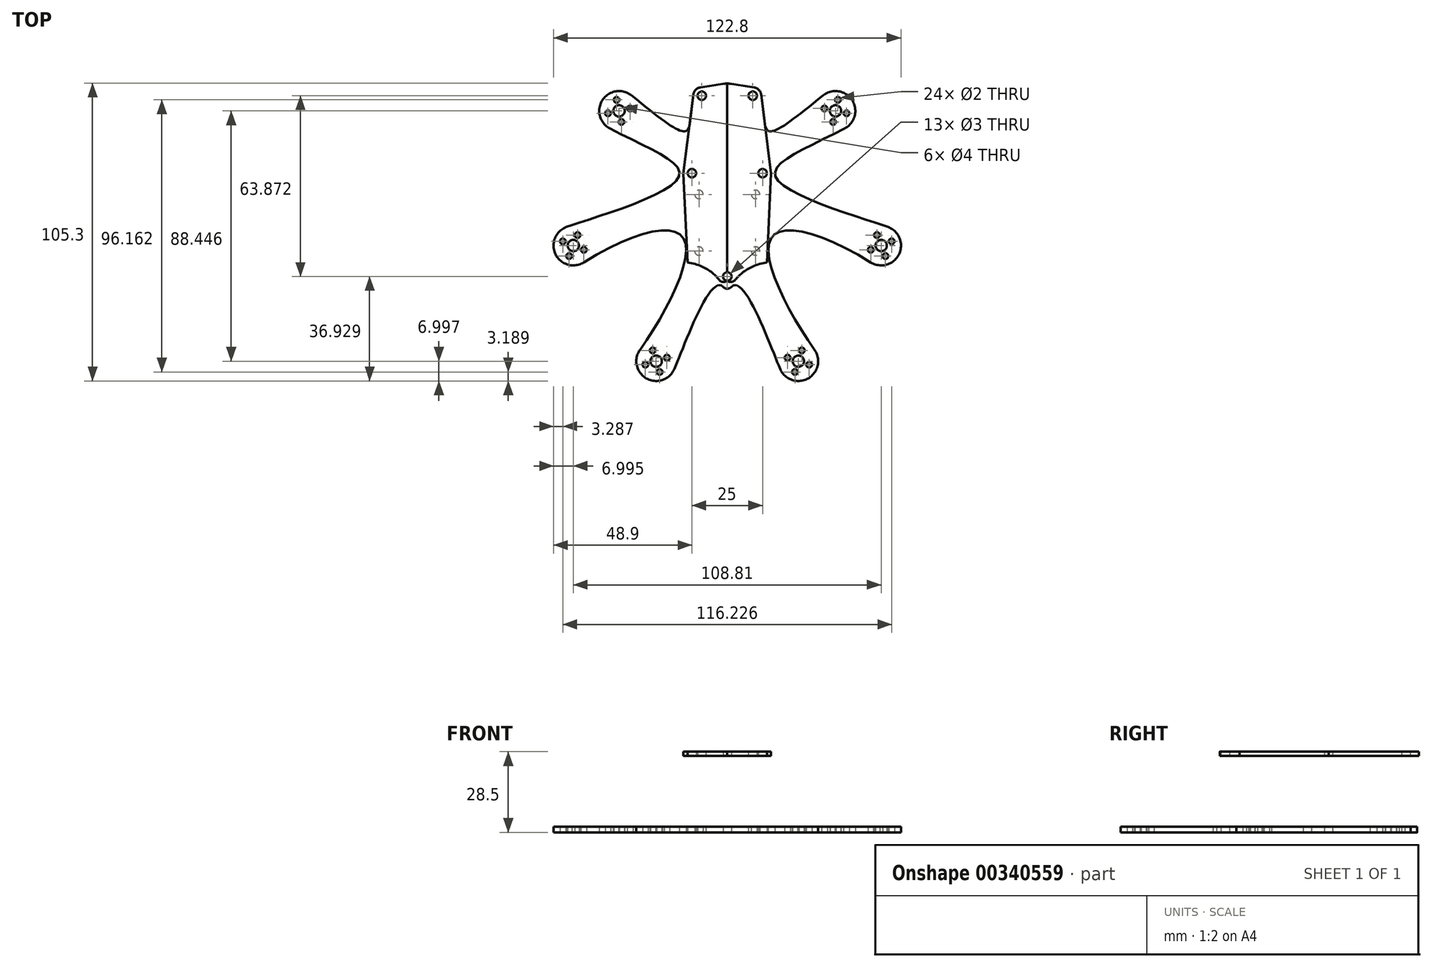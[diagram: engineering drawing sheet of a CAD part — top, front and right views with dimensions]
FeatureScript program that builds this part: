
annotation { "Feature Type Name" : "Feature", "Feature Type Description" : "" }
export const myFeature = defineFeature(function(context is Context, id is Id, definition is map)
    precondition{}
    {
        {
            var Q0;
            Q0=qCreatedBy(makeId("Top.planeOp"),FACE);
            var sketch = newSketch(context, id + "F0", { "sketchPlane" : qUnion([Q0])});
            skCircle(sketch, "E0", {"center": v(0, 0) * mm, "radius": 55 * mm, "construction": true});
            skCircle(sketch, "E1", {"center": v(-38.25, 39.52) * mm, "radius": 24.13 * mm, "construction": true});
            skCircle(sketch, "E2", {"center": v(-54.4, -8.07) * mm, "radius": 24.13 * mm, "construction": true});
            skCircle(sketch, "E3", {"center": v(-25.13, -48.92) * mm, "radius": 24.13 * mm, "construction": true});
            skLineSegment(sketch, "E4.bottom", {"start": v(13.5, -13.5) * mm, "end": v(-13.5, -13.5) * mm, "construction": true});
            skLineSegment(sketch, "E4.top", {"start": v(13.5, 13.5) * mm, "end": v(-13.5, 13.5) * mm, "construction": true});
            skLineSegment(sketch, "E4.left", {"start": v(13.5, -13.5) * mm, "end": v(13.5, 13.5) * mm, "construction": true});
            skLineSegment(sketch, "E4.right", {"start": v(-13.5, -13.5) * mm, "end": v(-13.5, 13.5) * mm, "construction": true});
            skLineSegment(sketch, "E5", {"start": v(-38.25, 39.52) * mm, "end": v(0, 15) * mm, "construction": true});
            skCircle(sketch, "E6", {"center": v(-38.25, 39.52) * mm, "radius": 7 * mm});
            skCircle(sketch, "E7", {"center": v(-54.4, -8.07) * mm, "radius": 7 * mm});
            skCircle(sketch, "E8", {"center": v(-25.13, -48.92) * mm, "radius": 7 * mm});
            skLineSegment(sketch, "E9", {"start": v(-26.46, 31.97) * mm, "end": v(-23.5, 36.6) * mm, "construction": true});
            skLineSegment(sketch, "E10", {"start": v(-23.5, 36.6) * mm, "end": v(-8.34, 26.88) * mm, "construction": true});
            skLineSegment(sketch, "E11", {"start": v(-8.34, 26.88) * mm, "end": v(-14.28, 17.62) * mm, "construction": true});
            skLineSegment(sketch, "E12", {"start": v(-14.28, 17.62) * mm, "end": v(-29.43, 27.34) * mm, "construction": true});
            skLineSegment(sketch, "E13", {"start": v(-29.43, 27.34) * mm, "end": v(-26.46, 31.97) * mm, "construction": true});
            skLineSegment(sketch, "E14", {"start": v(-54.4, -8.07) * mm, "end": v(0, 15) * mm, "construction": true});
            skLineSegment(sketch, "E15", {"start": v(-41.52, -2.6) * mm, "end": v(-43.66, 2.46) * mm, "construction": true});
            skLineSegment(sketch, "E16", {"start": v(-43.66, 2.46) * mm, "end": v(-27.1, 9.49) * mm, "construction": true});
            skLineSegment(sketch, "E17", {"start": v(-27.1, 9.49) * mm, "end": v(-22.8, -0.64) * mm, "construction": true});
            skLineSegment(sketch, "E18", {"start": v(-22.8, -0.64) * mm, "end": v(-39.37, -7.67) * mm, "construction": true});
            skLineSegment(sketch, "E19", {"start": v(-39.37, -7.67) * mm, "end": v(-41.52, -2.6) * mm, "construction": true});
            skLineSegment(sketch, "E20", {"start": v(-25.13, -48.92) * mm, "end": v(0, 0) * mm, "construction": true});
            skLineSegment(sketch, "E21", {"start": v(-18.73, -36.47) * mm, "end": v(-23.63, -33.96) * mm, "construction": true});
            skLineSegment(sketch, "E22", {"start": v(-23.63, -33.96) * mm, "end": v(-15.4, -17.95) * mm, "construction": true});
            skLineSegment(sketch, "E23", {"start": v(-15.4, -17.95) * mm, "end": v(-5.62, -22.97) * mm, "construction": true});
            skLineSegment(sketch, "E24", {"start": v(-5.62, -22.97) * mm, "end": v(-13.84, -38.98) * mm, "construction": true});
            skLineSegment(sketch, "E25", {"start": v(-13.84, -38.98) * mm, "end": v(-18.73, -36.47) * mm, "construction": true});
            skPoint(sketch, "E26", {"position": v(0, 13.5) * mm});
            skLineSegment(sketch, "E27", {"start": v(-14.28, 17.62) * mm, "end": v(-27.1, 9.49) * mm, "construction": true});
            skLineSegment(sketch, "E28", {"start": v(-22.8, -0.64) * mm, "end": v(-15.4, -17.95) * mm, "construction": true});
            skFitSpline(sketch, "E29", {"points": [v(-56.9, -1.53) * mm, v(-17.37, 15.66) * mm, v(-41.5, 33.32) * mm], "startDerivative": vector(36.2, 13.81) * mm, "endDerivative": vector(-89.8, 47.04) * mm});
            skFitSpline(sketch, "E30", {"points": [v(-50.68, -14) * mm, v(-15.32, -5.8) * mm, v(-30.82, -44.85) * mm], "startDerivative": vector(104.9, 65.91) * mm, "endDerivative": vector(-53.34, -74.52) * mm});
            skFitSpline(sketch, "E31", {"points": [v(-18.7, -51.71) * mm, v(0, -25.5) * mm], "startDerivative": vector(11.94, 27.48) * mm, "endDerivative": vector(12.67, -40.7) * mm});
            skLineSegment(sketch, "E32.bottom", {"start": v(10, 39.13) * mm, "end": v(-10, 39.13) * mm, "construction": true});
            skLineSegment(sketch, "E32.top", {"start": v(10, 29.13) * mm, "end": v(-10, 29.13) * mm, "construction": true});
            skLineSegment(sketch, "E32.left", {"start": v(10, 39.13) * mm, "end": v(10, 29.13) * mm, "construction": true});
            skLineSegment(sketch, "E32.right", {"start": v(-10, 39.13) * mm, "end": v(-10, 29.13) * mm, "construction": true});
            skPoint(sketch, "E32.middle", {"position": v(0, 34.13) * mm});
            skCircle(sketch, "E33", {"center": v(-9, 44.88) * mm, "radius": 2.5 * mm, "construction": true});
            skCircle(sketch, "E34", {"center": v(0, -19) * mm, "radius": 2.5 * mm, "construction": true});
            skCircle(sketch, "E35", {"center": v(-12.5, 17.5) * mm, "radius": 2.5 * mm, "construction": true});
            skLineSegment(sketch, "E36", {"start": v(-11.98, 45.26) * mm, "end": v(-15.5, 17.5) * mm});
            skLineSegment(sketch, "E37", {"start": v(-9.48, 47.84) * mm, "end": v(0, 49.38) * mm});
            skArc(sketch, "E38", {"start": v(-9, 41.88) * mm, "mid": v(-11.12, 47) * mm, "end": v(-6, 44.88) * mm});
            skFitSpline(sketch, "E39", {"points": [v(-33.86, 44.98) * mm, v(-13.3, 34.86) * mm], "startDerivative": vector(41.25, -33.22) * mm, "endDerivative": vector(2.26, 17.82) * mm});
            skCircle(sketch, "E40", {"center": v(0, -19) * mm, "radius": 1.5 * mm});
            skCircle(sketch, "E41", {"center": v(-12.5, 17.5) * mm, "radius": 1.5 * mm});
            skCircle(sketch, "E42", {"center": v(-9, 44.88) * mm, "radius": 1.5 * mm});
            skLineSegment(sketch, "E43", {"start": v(-15.5, 17.5) * mm, "end": v(-14.02, -14) * mm});
            skFitSpline(sketch, "E44", {"points": [v(-14.02, -14) * mm, v(0, -25.5) * mm], "startDerivative": vector(26.66, -3.76) * mm, "endDerivative": vector(2.8, -10.93) * mm});
            skLineSegment(sketch, "E45", {"start": v(0, 49.38) * mm, "end": v(0, -25.5) * mm});
            skCircle(sketch, "E46", {"center": v(-38.25, 39.52) * mm, "radius": 2 * mm});
            skCircle(sketch, "E47", {"center": v(-54.4, -8.07) * mm, "radius": 2 * mm});
            skCircle(sketch, "E48", {"center": v(-25.13, -48.92) * mm, "radius": 2 * mm});
            skLineSegment(sketch, "E49", {"start": v(-38.25, 39.52) * mm, "end": v(-34.34, 40.38) * mm, "construction": true});
            skCircle(sketch, "E50", {"center": v(-34.34, 40.38) * mm, "radius": 1 * mm});
            skCircle(sketch, "E51.1.0", {"center": v(-39.1, 43.43) * mm, "radius": 1 * mm});
            skCircle(sketch, "E51.2.0", {"center": v(-42.16, 38.67) * mm, "radius": 1 * mm});
            skCircle(sketch, "E51.3.0", {"center": v(-37.4, 35.62) * mm, "radius": 1 * mm});
            skLineSegment(sketch, "E52", {"start": v(-54.4, -8.07) * mm, "end": v(-52.9, -4.36) * mm, "construction": true});
            skCircle(sketch, "E53", {"center": v(-52.9, -4.36) * mm, "radius": 1 * mm});
            skCircle(sketch, "E54.1.0", {"center": v(-58.11, -6.57) * mm, "radius": 1 * mm});
            skCircle(sketch, "E54.2.0", {"center": v(-55.9, -11.78) * mm, "radius": 1 * mm});
            skCircle(sketch, "E54.3.0", {"center": v(-50.7, -9.57) * mm, "radius": 1 * mm});
            skLineSegment(sketch, "E55", {"start": v(-25.13, -48.92) * mm, "end": v(-26.35, -45.11) * mm, "construction": true});
            skCircle(sketch, "E56", {"center": v(-26.35, -45.11) * mm, "radius": 1 * mm});
            skCircle(sketch, "E57.1.0", {"center": v(-28.94, -50.15) * mm, "radius": 1 * mm});
            skCircle(sketch, "E57.2.0", {"center": v(-23.9, -52.73) * mm, "radius": 1 * mm});
            skCircle(sketch, "E57.3.0", {"center": v(-21.32, -47.7) * mm, "radius": 1 * mm});
            skCircle(sketch, "E58", {"center": v(-10, 10) * mm, "radius": 1.5 * mm});
            skCircle(sketch, "E59", {"center": v(-10, -10) * mm, "radius": 1.5 * mm});
            skSolve(sketch);
        }
        {
            var Q0;
            {var subQ0=sQuery(id+"F0.wireOp",EDGE,"E6");var subQ1=makeQuery(id+"F0.imprint","INTERSECT",VERTEX,{"derivedFrom":[subQ0,sQuery(id+"F0.wireOp",EDGE,"E29")]});Q0=makeQuery(id+"F0.imprint","IMPRINT",FACE,{"disambiguationData":[TD([[makeQuery(id+"F0.imprint","IMPRINT",EDGE,{"disambiguationData":[TD([[subQ1,1.0]])],"derivedFrom":subQ0}),1.0]])]});}
            var Q1;
            {var subQ0=sQuery(id+"F0.wireOp",EDGE,"E7");var subQ1=makeQuery(id+"F0.imprint","INTERSECT",VERTEX,{"derivedFrom":[subQ0,sQuery(id+"F0.wireOp",EDGE,"E29")]});Q1=makeQuery(id+"F0.imprint","IMPRINT",FACE,{"disambiguationData":[TD([[makeQuery(id+"F0.imprint","IMPRINT",EDGE,{"disambiguationData":[TD([[subQ1,-1.0]])],"derivedFrom":subQ0}),1.0]])]});}
            var Q2;
            {var subQ0=sQuery(id+"F0.wireOp",EDGE,"E8");var subQ1=makeQuery(id+"F0.imprint","INTERSECT",VERTEX,{"derivedFrom":[subQ0,sQuery(id+"F0.wireOp",EDGE,"E30")]});Q2=makeQuery(id+"F0.imprint","IMPRINT",FACE,{"disambiguationData":[TD([[makeQuery(id+"F0.imprint","IMPRINT",EDGE,{"disambiguationData":[TD([[subQ1,-1.0]])],"derivedFrom":subQ0}),1.0]])]});}
            var Q3;
            {var subQ3=sQuery(id+"F0.wireOp",EDGE,"E29");Q3=makeQuery(id+"F0.imprint","IMPRINT",FACE,{"disambiguationData":[TD([[makeQuery(id+"F0.imprint","IMPRINT",EDGE,{"derivedFrom":subQ3}),-1.0]])]});}
            var Q4;
            {var subQ6=sQuery(id+"F0.wireOp",EDGE,"E37");Q4=makeQuery(id+"F0.imprint","IMPRINT",FACE,{"disambiguationData":[TD([[makeQuery(id+"F0.imprint","IMPRINT",EDGE,{"derivedFrom":subQ6}),-1.0]])]});}
            extrude(context, id + "F1", {"entities" : qUnion([Q0, Q1, Q2, Q3, Q4]), "depth" : 2 * mm});
        }
        {
            var Q0;
            Q0=makeQuery(id+"F1.opExtrude","SWEPT_BODY",BODY,{"disambiguationData":[OSD([sQuery(id+"F0.wireOp",EDGE,"E6"),sQuery(id+"F0.wireOp",EDGE,"E7"),sQuery(id+"F0.wireOp",EDGE,"E8"),sQuery(id+"F0.wireOp",EDGE,"E29"),sQuery(id+"F0.wireOp",EDGE,"E30"),sQuery(id+"F0.wireOp",EDGE,"E31"),sQuery(id+"F0.wireOp",EDGE,"E36"),sQuery(id+"F0.wireOp",EDGE,"E37"),sQuery(id+"F0.wireOp",EDGE,"E38"),sQuery(id+"F0.wireOp",EDGE,"E39"),sQuery(id+"F0.wireOp",EDGE,"E40"),sQuery(id+"F0.wireOp",EDGE,"E41"),sQuery(id+"F0.wireOp",EDGE,"E42"),sQuery(id+"F0.wireOp",EDGE,"E45"),sQuery(id+"F0.wireOp",EDGE,"E46"),sQuery(id+"F0.wireOp",EDGE,"E47"),sQuery(id+"F0.wireOp",EDGE,"E48"),sQuery(id+"F0.wireOp",EDGE,"E50"),sQuery(id+"F0.wireOp",EDGE,"E51.1.0"),sQuery(id+"F0.wireOp",EDGE,"E51.2.0"),sQuery(id+"F0.wireOp",EDGE,"E51.3.0"),sQuery(id+"F0.wireOp",EDGE,"E53"),sQuery(id+"F0.wireOp",EDGE,"E54.1.0"),sQuery(id+"F0.wireOp",EDGE,"E54.2.0"),sQuery(id+"F0.wireOp",EDGE,"E54.3.0"),sQuery(id+"F0.wireOp",EDGE,"E56"),sQuery(id+"F0.wireOp",EDGE,"E57.1.0"),sQuery(id+"F0.wireOp",EDGE,"E57.2.0"),sQuery(id+"F0.wireOp",EDGE,"E57.3.0"),sQuery(id+"F0.wireOp",EDGE,"E58"),sQuery(id+"F0.wireOp",EDGE,"E59")])]});
            var Q1;
            {var subQ0=sQuery(id+"F0.wireOp",EDGE,"E45");Q1=makeQuery(id+"F1.opExtrude","SWEPT_FACE",FACE,{"disambiguationData":[OSD([subQ0]),TDD([makeQuery(id+"F0.imprint","IMPRINT",EDGE,{"disambiguationData":[TD([[makeQuery(id+"F0.imprint","INTERSECT",VERTEX,{"derivedFrom":[sQuery(id+"F0.wireOp",EDGE,"E37"),subQ0]}),-1.0]])],"derivedFrom":subQ0})])]});}
            mirror(context, id + "F2", {"operationType" : NewBodyOperationType.ADD, "entities" : qUnion([Q0]), "mirrorPlane" : qUnion([Q1])});
        }
        {
            var Q0;
            {var subQ6=sQuery(id+"F0.wireOp",EDGE,"E37");Q0=makeQuery(id+"F0.imprint","IMPRINT",FACE,{"disambiguationData":[TD([[makeQuery(id+"F0.imprint","IMPRINT",EDGE,{"derivedFrom":subQ6}),-1.0]])]});}
            var Q1;
            Q1=makeQuery(id+"F0.imprint","IMPRINT",FACE,{"disambiguationData":[TD([[makeQuery(id+"F0.imprint","IMPRINT",EDGE,{"derivedFrom":sQuery(id+"F0.wireOp",EDGE,"E59")}),1.0]])]});
            var Q2;
            Q2=makeQuery(id+"F0.imprint","IMPRINT",FACE,{"disambiguationData":[TD([[makeQuery(id+"F0.imprint","IMPRINT",EDGE,{"derivedFrom":sQuery(id+"F0.wireOp",EDGE,"E58")}),1.0]])]});
            extrude(context, id + "F3", {"entities" : qUnion([Q0, Q1, Q2]), "depth" : 28.5 * mm, "hasSecondDirection" : true, "secondDirectionOppositeDirection" : false, "secondDirectionDepth" : 27 * mm});
        }
        {
            var Q0;
            Q0=makeQuery(id+"F3.opExtrude","SWEPT_BODY",BODY,{"disambiguationData":[OSD([sQuery(id+"F0.wireOp",EDGE,"E36"),sQuery(id+"F0.wireOp",EDGE,"E37"),sQuery(id+"F0.wireOp",EDGE,"E38"),sQuery(id+"F0.wireOp",EDGE,"E40"),sQuery(id+"F0.wireOp",EDGE,"E41"),sQuery(id+"F0.wireOp",EDGE,"E42"),sQuery(id+"F0.wireOp",EDGE,"E43"),sQuery(id+"F0.wireOp",EDGE,"E44"),sQuery(id+"F0.wireOp",EDGE,"E45")])]});
            var Q1;
            {var subQ0=sQuery(id+"F0.wireOp",EDGE,"E45");Q1=makeQuery(id+"F3.opExtrude","SWEPT_FACE",FACE,{"disambiguationData":[OSD([subQ0]),TDD([makeQuery(id+"F0.imprint","IMPRINT",EDGE,{"disambiguationData":[TD([[makeQuery(id+"F0.imprint","INTERSECT",VERTEX,{"derivedFrom":[sQuery(id+"F0.wireOp",EDGE,"E37"),subQ0]}),-1.0]])],"derivedFrom":subQ0})])]});}
            mirror(context, id + "F4", {"operationType" : NewBodyOperationType.ADD, "entities" : qUnion([Q0]), "mirrorPlane" : qUnion([Q1])});
        }
        {
            var Q0;
            {var subQ0=makeQuery(id+"F1.opExtrude","SWEPT_EDGE",EDGE,{"disambiguationData":[OSD([sQuery(id+"F0.wireOp",EDGE,"E31"),sQuery(id+"F0.wireOp",EDGE,"E44"),sQuery(id+"F0.wireOp",EDGE,"E45")])]});Q0=makeQuery(id+"F2.boolean.opBoolean","MERGE",EDGE,{"derivedFrom":[subQ0,makeQuery(id+"F2.opPattern","COPY",EDGE,{"derivedFrom":subQ0,"instanceName":"1"})]});}
            var Q1;
            {var subQ0=makeQuery(id+"F3.opExtrude","SWEPT_EDGE",EDGE,{"disambiguationData":[OSD([sQuery(id+"F0.wireOp",EDGE,"E31"),sQuery(id+"F0.wireOp",EDGE,"E44"),sQuery(id+"F0.wireOp",EDGE,"E45")])]});Q1=makeQuery(id+"F4.boolean.opBoolean","MERGE",EDGE,{"derivedFrom":[subQ0,makeQuery(id+"F4.opPattern","COPY",EDGE,{"derivedFrom":subQ0,"instanceName":"1"})]});}
            fillet(context, id + "F5", {"entities" : qUnion([Q0, Q1]), "radius" : 2 * mm, "tangentPropagation" : true, "allowEdgeOverflow" : false});
        }
        {
            var Q0;
            {var subQ0=makeQuery(id+"F1.opExtrude","SWEPT_EDGE",EDGE,{"disambiguationData":[OSD([sQuery(id+"F0.wireOp",EDGE,"E37"),sQuery(id+"F0.wireOp",EDGE,"E45")])]});Q0=makeQuery(id+"F2.boolean.opBoolean","MERGE",EDGE,{"derivedFrom":[subQ0,makeQuery(id+"F2.opPattern","COPY",EDGE,{"derivedFrom":subQ0,"instanceName":"1"})]});}
            var Q1;
            {var subQ0=makeQuery(id+"F3.opExtrude","SWEPT_EDGE",EDGE,{"disambiguationData":[OSD([sQuery(id+"F0.wireOp",EDGE,"E37"),sQuery(id+"F0.wireOp",EDGE,"E45")])]});Q1=makeQuery(id+"F4.boolean.opBoolean","MERGE",EDGE,{"derivedFrom":[subQ0,makeQuery(id+"F4.opPattern","COPY",EDGE,{"derivedFrom":subQ0,"instanceName":"1"})]});}
            fillet(context, id + "F6", {"entities" : qUnion([Q0, Q1]), "radius" : 40 * mm, "tangentPropagation" : true, "allowEdgeOverflow" : false});
        }
    });
